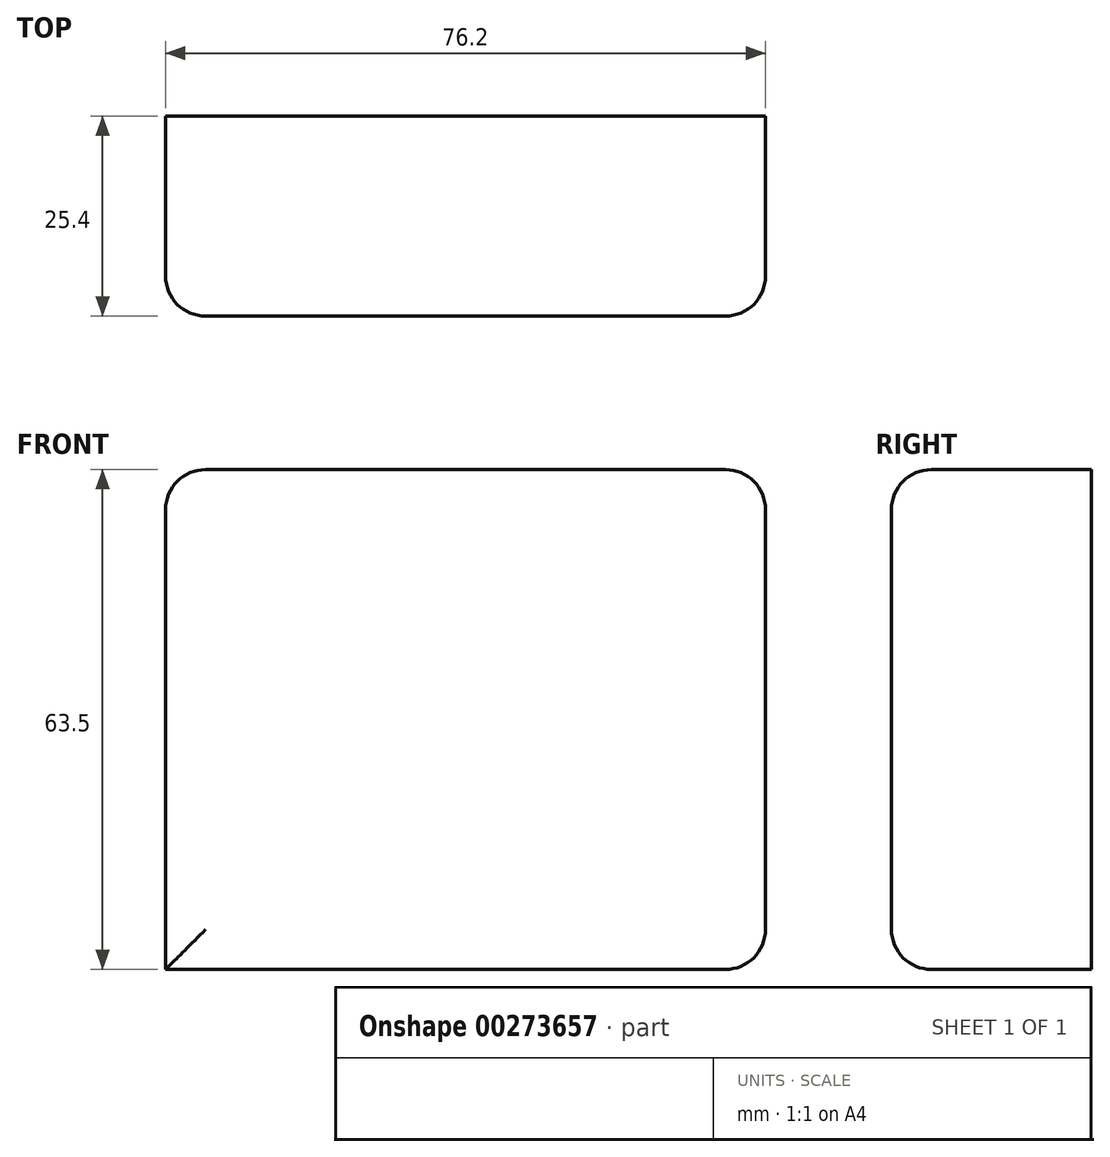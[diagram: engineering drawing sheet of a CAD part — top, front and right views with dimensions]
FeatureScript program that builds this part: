
annotation { "Feature Type Name" : "Feature", "Feature Type Description" : "" }
export const myFeature = defineFeature(function(context is Context, id is Id, definition is map)
    precondition{}
    {
        {
            var Q0;
            Q0=qCreatedBy(makeId("Front.planeOp"),FACE);
            var sketch = newSketch(context, id + "F0", { "sketchPlane" : qUnion([Q0])});
            skLineSegment(sketch, "E0.bottom", {"start": v(-26.42, 31.07) * mm, "end": v(49.78, 31.07) * mm});
            skLineSegment(sketch, "E0.top", {"start": v(-26.42, -32.43) * mm, "end": v(49.78, -32.43) * mm});
            skLineSegment(sketch, "E0.left", {"start": v(-26.42, 31.07) * mm, "end": v(-26.42, -32.43) * mm});
            skLineSegment(sketch, "E0.right", {"start": v(49.78, 31.07) * mm, "end": v(49.78, -32.43) * mm});
            skSolve(sketch);
        }
        {
            var Q0;
            Q0=makeQuery(id+"F0.imprint","IMPRINT",FACE,{"disambiguationData":[TD([[makeQuery(id+"F0.imprint","IMPRINT",EDGE,{"derivedFrom":sQuery(id+"F0.wireOp",EDGE,"E0.bottom")}),-1.0]])]});
            extrude(context, id + "F1", {"entities" : qUnion([Q0]), "depth" : 25.4 * mm});
        }
        {
            var Q0;
            Q0=makeQuery(id+"F1.opExtrude","SWEPT_EDGE",EDGE,{"disambiguationData":[OSD([sQuery(id+"F0.wireOp",EDGE,"E0.bottom"),sQuery(id+"F0.wireOp",EDGE,"E0.right")])]});
            var Q1;
            Q1=makeQuery(id+"F1.opExtrude","SWEPT_EDGE",EDGE,{"disambiguationData":[OSD([sQuery(id+"F0.wireOp",EDGE,"E0.bottom"),sQuery(id+"F0.wireOp",EDGE,"E0.left")])]});
            var Q2;
            Q2=makeQuery(id+"F1.opExtrude","SWEPT_EDGE",EDGE,{"disambiguationData":[OSD([sQuery(id+"F0.wireOp",EDGE,"E0.top"),sQuery(id+"F0.wireOp",EDGE,"E0.right")])]});
            var Q3;
            Q3=makeQuery(id+"F1.opExtrude","CAP_FACE",FACE,{"disambiguationData":[OSD([sQuery(id+"F0.wireOp",EDGE,"E0.bottom"),sQuery(id+"F0.wireOp",EDGE,"E0.top"),sQuery(id+"F0.wireOp",EDGE,"E0.left"),sQuery(id+"F0.wireOp",EDGE,"E0.right")])],"isStart":false});
            fillet(context, id + "F2", {"entities" : qUnion([Q0, Q1, Q2, Q3]), "radius" : 5.08 * mm, "tangentPropagation" : true, "allowEdgeOverflow" : false});
        }
    });
